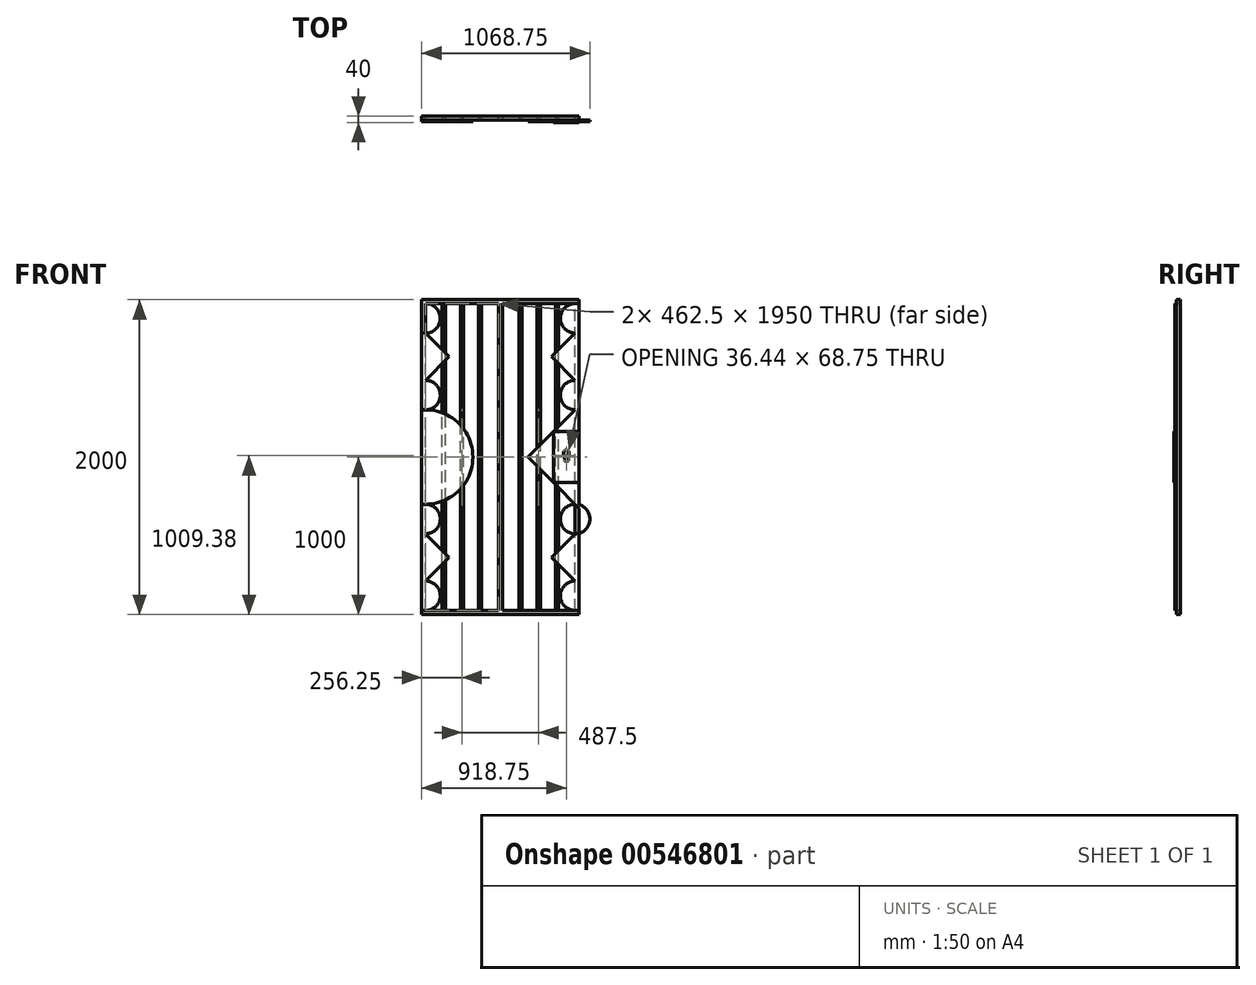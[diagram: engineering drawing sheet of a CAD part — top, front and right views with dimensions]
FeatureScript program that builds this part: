
annotation { "Feature Type Name" : "Feature", "Feature Type Description" : "" }
export const myFeature = defineFeature(function(context is Context, id is Id, definition is map)
    precondition{}
    {
        {
            var Q0;
            Q0=qCreatedBy(makeId("Front.planeOp"),FACE);
            var sketch = newSketch(context, id + "F0", { "sketchPlane" : qUnion([Q0])});
            skLineSegment(sketch, "E0.bottom", {"start": v(500, 12.5) * mm, "end": v(-500, 12.5) * mm});
            skLineSegment(sketch, "E0.top", {"start": v(500, -12.5) * mm, "end": v(-500, -12.5) * mm});
            skLineSegment(sketch, "E0.left", {"start": v(500, 12.5) * mm, "end": v(500, -12.5) * mm});
            skLineSegment(sketch, "E0.right", {"start": v(-500, 12.5) * mm, "end": v(-500, -12.5) * mm});
            skPoint(sketch, "E0.middle", {"position": v(0, 0) * mm});
            skLineSegment(sketch, "E1.bottom", {"start": v(-500, -12.5) * mm, "end": v(-475, -12.5) * mm});
            skLineSegment(sketch, "E1.top", {"start": v(-500, 1987.5) * mm, "end": v(-475, 1987.5) * mm});
            skLineSegment(sketch, "E1.left", {"start": v(-500, -12.5) * mm, "end": v(-500, 1987.5) * mm});
            skLineSegment(sketch, "E1.right", {"start": v(-475, -12.5) * mm, "end": v(-475, 1987.5) * mm});
            skLineSegment(sketch, "E2.bottom", {"start": v(500, -12.5) * mm, "end": v(475, -12.5) * mm});
            skLineSegment(sketch, "E2.top", {"start": v(500, 1987.5) * mm, "end": v(475, 1987.5) * mm});
            skLineSegment(sketch, "E2.left", {"start": v(500, -12.5) * mm, "end": v(500, 1987.5) * mm});
            skLineSegment(sketch, "E2.right", {"start": v(475, -12.5) * mm, "end": v(475, 1987.5) * mm});
            skLineSegment(sketch, "E3.bottom", {"start": v(500, 1987.5) * mm, "end": v(-500, 1987.5) * mm});
            skLineSegment(sketch, "E3.top", {"start": v(500, 1962.5) * mm, "end": v(-500, 1962.5) * mm});
            skLineSegment(sketch, "E3.left", {"start": v(500, 1987.5) * mm, "end": v(500, 1962.5) * mm});
            skLineSegment(sketch, "E3.right", {"start": v(-500, 1987.5) * mm, "end": v(-500, 1962.5) * mm});
            skSolve(sketch);
        }
        {
            var Q0;
            Q0 = qSketchRegion(id + "F0", true);
            extrude(context, id + "F1", {"entities" : qUnion([Q0]), "depth" : 25 * mm, "offsetDistance" : 25 * mm});
        }
        {
            var Q0;
            Q0=qCreatedBy(makeId("Top.planeOp"),FACE);
            var sketch = newSketch(context, id + "F2", { "sketchPlane" : qUnion([Q0])});
            skLineSegment(sketch, "E4.bottom", {"start": v(0, 0) * mm, "end": v(12.5, 0) * mm});
            skLineSegment(sketch, "E4.top", {"start": v(0, -25) * mm, "end": v(12.5, -25) * mm});
            skLineSegment(sketch, "E4.right", {"start": v(12.5, 0) * mm, "end": v(12.5, -25) * mm});
            skLineSegment(sketch, "E5.bottom", {"start": v(12.5, -25) * mm, "end": v(-12.5, -25) * mm});
            skLineSegment(sketch, "E5.top", {"start": v(12.5, 0) * mm, "end": v(-12.5, 0) * mm});
            skLineSegment(sketch, "E5.left", {"start": v(12.5, -25) * mm, "end": v(12.5, 0) * mm});
            skLineSegment(sketch, "E5.right", {"start": v(-12.5, -25) * mm, "end": v(-12.5, 0) * mm});
            skSolve(sketch);
        }
        {
            var Q0;
            Q0 = qSketchRegion(id + "F2", true);
            extrude(context, id + "F3", {"entities" : qUnion([Q0]), "operationType" : NewBodyOperationType.ADD, "depth" : 1975 * mm, "offsetDistance" : 25 * mm});
        }
        {
            var Q0;
            Q0=makeQuery(id+"F3.boolean.opBoolean","MERGE",FACE,{"derivedFrom":[makeQuery(id+"F1.opExtrude","CAP_FACE",FACE,{"disambiguationData":[OSD([sQuery(id+"F0.wireOp",EDGE,"E0.bottom"),sQuery(id+"F0.wireOp",EDGE,"E0.top"),sQuery(id+"F0.wireOp",EDGE,"E1.bottom"),sQuery(id+"F0.wireOp",EDGE,"E1.left"),sQuery(id+"F0.wireOp",EDGE,"E1.right"),sQuery(id+"F0.wireOp",EDGE,"E2.bottom"),sQuery(id+"F0.wireOp",EDGE,"E2.left"),sQuery(id+"F0.wireOp",EDGE,"E2.right"),sQuery(id+"F0.wireOp",EDGE,"E3.bottom"),sQuery(id+"F0.wireOp",EDGE,"E3.top"),sQuery(id+"F0.wireOp",EDGE,"E3.left"),sQuery(id+"F0.wireOp",EDGE,"E3.right")])],"isStart":false}),makeQuery(id+"F3.opExtrude","SWEPT_FACE",FACE,{"disambiguationData":[OSD([sQuery(id+"F2.wireOp",EDGE,"E5.bottom")])]})]});
            var sketch = newSketch(context, id + "F4", { "sketchPlane" : qUnion([Q0])});
            skLineSegment(sketch, "E6", {"start": v(475, 987.5) * mm, "end": v(475, 1187.5) * mm, "construction": true});
            skLineSegment(sketch, "E7", {"start": v(475, 987.5) * mm, "end": v(475, 787.5) * mm, "construction": true});
            skLineSegment(sketch, "E8", {"start": v(475, 987.5) * mm, "end": v(275, 987.5) * mm, "construction": true});
            skLineSegment(sketch, "E9", {"start": v(275, 987.5) * mm, "end": v(175, 987.5) * mm, "construction": true});
            skLineSegment(sketch, "E10", {"start": v(475, 1187.5) * mm, "end": v(475, 1287.5) * mm, "construction": true});
            skLineSegment(sketch, "E11", {"start": v(475, 787.5) * mm, "end": v(475, 687.5) * mm, "construction": true});
            skLineSegment(sketch, "E12", {"start": v(475, 687.5) * mm, "end": v(175, 987.5) * mm});
            skLineSegment(sketch, "E13", {"start": v(475, 1287.5) * mm, "end": v(175, 987.5) * mm});
            skCircle(sketch, "E14", {"center": v(-475, 987.5) * mm, "radius": 300 * mm});
            skLineSegment(sketch, "E15", {"start": v(475, 1287.5) * mm, "end": v(500, 1312.5) * mm});
            skLineSegment(sketch, "E16", {"start": v(175, 987.5) * mm, "end": v(505.2, 657.3) * mm});
            skLineSegment(sketch, "E17", {"start": v(475, 12.5) * mm, "end": v(500, 12.5) * mm, "construction": true});
            skLineSegment(sketch, "E18", {"start": v(-475, 12.5) * mm, "end": v(-500, 12.5) * mm, "construction": true});
            skLineSegment(sketch, "E19", {"start": v(475, 1962.5) * mm, "end": v(500, 1962.5) * mm, "construction": true});
            skLineSegment(sketch, "E20", {"start": v(-475, 1962.5) * mm, "end": v(-500, 1962.5) * mm, "construction": true});
            skLineSegment(sketch, "E21", {"start": v(-475, 12.5) * mm, "end": v(-475, 687.5) * mm, "construction": true});
            skLineSegment(sketch, "E22", {"start": v(475, 12.5) * mm, "end": v(475, 687.5) * mm, "construction": true});
            skLineSegment(sketch, "E23", {"start": v(475, 1287.5) * mm, "end": v(475, 1962.5) * mm, "construction": true});
            skLineSegment(sketch, "E24", {"start": v(-475, 1962.5) * mm, "end": v(-475, 1287.5) * mm, "construction": true});
            skLineSegment(sketch, "E25", {"start": v(-475, 350) * mm, "end": v(-500, 350) * mm, "construction": true});
            skLineSegment(sketch, "E26", {"start": v(-475, 350) * mm, "end": v(-475, 500) * mm});
            skLineSegment(sketch, "E27", {"start": v(-475, 350) * mm, "end": v(-325, 350) * mm});
            skLineSegment(sketch, "E28", {"start": v(-475, 350) * mm, "end": v(-475, 200) * mm});
            skLineSegment(sketch, "E29", {"start": v(-475, 200) * mm, "end": v(-325, 350) * mm});
            skLineSegment(sketch, "E30", {"start": v(-325, 350) * mm, "end": v(-475, 500) * mm});
            skLineSegment(sketch, "E31", {"start": v(-325, 350) * mm, "end": v(-500, 525) * mm});
            skLineSegment(sketch, "E32", {"start": v(-325, 350) * mm, "end": v(-500, 175) * mm});
            skLineSegment(sketch, "E33", {"start": v(475, 350) * mm, "end": v(475, 500) * mm});
            skLineSegment(sketch, "E34", {"start": v(475, 350) * mm, "end": v(325, 350) * mm});
            skLineSegment(sketch, "E35", {"start": v(475, 350) * mm, "end": v(475, 200) * mm});
            skLineSegment(sketch, "E36", {"start": v(475, 200) * mm, "end": v(325, 350) * mm});
            skLineSegment(sketch, "E37", {"start": v(475, 500) * mm, "end": v(325, 350) * mm});
            skLineSegment(sketch, "E38", {"start": v(325, 350) * mm, "end": v(500, 175) * mm});
            skLineSegment(sketch, "E39", {"start": v(325, 350) * mm, "end": v(500, 525) * mm});
            skLineSegment(sketch, "E40", {"start": v(475, 1625) * mm, "end": v(325, 1625) * mm});
            skPoint(sketch, "E40.endSnap0", {"position": v(475, 1625) * mm});
            skLineSegment(sketch, "E41", {"start": v(475, 1625) * mm, "end": v(475, 1775) * mm});
            skLineSegment(sketch, "E42", {"start": v(475, 1775) * mm, "end": v(475, 1475) * mm});
            skLineSegment(sketch, "E43", {"start": v(475, 1475) * mm, "end": v(325, 1625) * mm});
            skLineSegment(sketch, "E44", {"start": v(475, 1775) * mm, "end": v(325, 1625) * mm});
            skLineSegment(sketch, "E45", {"start": v(325, 1625) * mm, "end": v(500, 1450) * mm});
            skLineSegment(sketch, "E46", {"start": v(325, 1625) * mm, "end": v(500, 1800) * mm});
            skLineSegment(sketch, "E47", {"start": v(-475, 1625) * mm, "end": v(-325, 1625) * mm});
            skLineSegment(sketch, "E48", {"start": v(-475, 1625) * mm, "end": v(-475, 1475) * mm});
            skLineSegment(sketch, "E49", {"start": v(-475, 1475) * mm, "end": v(-475, 1775) * mm});
            skLineSegment(sketch, "E50", {"start": v(-475, 1775) * mm, "end": v(-325, 1625) * mm});
            skLineSegment(sketch, "E51", {"start": v(-325, 1625) * mm, "end": v(-500, 1800) * mm});
            skLineSegment(sketch, "E52", {"start": v(-500, 1800) * mm, "end": v(-325, 1625) * mm});
            skLineSegment(sketch, "E53", {"start": v(-325, 1625) * mm, "end": v(-500, 1450) * mm});
            skLineSegment(sketch, "E54", {"start": v(500, 662.5) * mm, "end": v(500, 525) * mm});
            skLineSegment(sketch, "E55", {"start": v(475, 687.5) * mm, "end": v(475, 500) * mm, "construction": true});
            skCircle(sketch, "E56", {"center": v(475, 593.75) * mm, "radius": 93.75 * mm});
            skLineSegment(sketch, "E57", {"start": v(475, 200) * mm, "end": v(475, 12.5) * mm, "construction": true});
            skCircle(sketch, "E58", {"center": v(475, 106.25) * mm, "radius": 93.75 * mm});
            skLineSegment(sketch, "E59", {"start": v(475, 1475) * mm, "end": v(475, 1287.5) * mm, "construction": true});
            skLineSegment(sketch, "E60", {"start": v(475, 1775) * mm, "end": v(475, 1962.5) * mm, "construction": true});
            skLineSegment(sketch, "E61", {"start": v(-475, 1962.5) * mm, "end": v(-475, 1775) * mm, "construction": true});
            skLineSegment(sketch, "E62", {"start": v(-475, 1475) * mm, "end": v(-475, 1287.5) * mm, "construction": true});
            skLineSegment(sketch, "E63", {"start": v(-475, 687.5) * mm, "end": v(-475, 500) * mm, "construction": true});
            skLineSegment(sketch, "E64", {"start": v(-475, 200) * mm, "end": v(-475, 12.5) * mm, "construction": true});
            skCircle(sketch, "E65", {"center": v(-475, 106.25) * mm, "radius": 93.75 * mm});
            skCircle(sketch, "E66", {"center": v(-475, 593.75) * mm, "radius": 93.75 * mm});
            skCircle(sketch, "E67", {"center": v(-475, 1381.25) * mm, "radius": 93.75 * mm});
            skCircle(sketch, "E68", {"center": v(-475, 1868.75) * mm, "radius": 93.75 * mm});
            skCircle(sketch, "E69", {"center": v(475, 1868.75) * mm, "radius": 93.75 * mm});
            skCircle(sketch, "E70", {"center": v(475, 1381.25) * mm, "radius": 93.75 * mm});
            skSolve(sketch);
        }
        {
            var Q0;
            {var subQ0=sQuery(id+"F4.wireOp",EDGE,"E14");var subQ1=makeQuery(id+"F1.opExtrude","CAP_EDGE",EDGE,{"disambiguationData":[OSD([sQuery(id+"F0.wireOp",EDGE,"E1.left"),sQuery(id+"F0.wireOp",EDGE,"E3.right")])],"isStart":false});var subQ2=makeQuery(id+"F4.imprint","INTERSECT",VERTEX,{"disambiguationData":[OD(0.0)],"derivedFrom":[subQ1,subQ0]});Q0=makeQuery(id+"F4.imprint","IMPRINT",FACE,{"disambiguationData":[TD([[makeQuery(id+"F4.imprint","IMPRINT",EDGE,{"disambiguationData":[TD([[subQ2,1.0]])],"derivedFrom":subQ0}),1.0]])]});}
            var Q1;
            {var subQ0=sQuery(id+"F4.wireOp",EDGE,"E14");var subQ1=makeQuery(id+"F1.opExtrude","CAP_EDGE",EDGE,{"disambiguationData":[OSD([sQuery(id+"F0.wireOp",EDGE,"E1.right")])],"isStart":false});var subQ2=makeQuery(id+"F4.imprint","INTERSECT",VERTEX,{"derivedFrom":[subQ1,subQ0,sQuery(id+"F4.wireOp",EDGE,"E67")]});Q1=makeQuery(id+"F4.imprint","IMPRINT",FACE,{"disambiguationData":[TD([[makeQuery(id+"F4.imprint","IMPRINT",EDGE,{"disambiguationData":[TD([[subQ2,1.0]])],"derivedFrom":subQ0}),1.0]])]});}
            var Q2;
            {var subQ1=sQuery(id+"F4.wireOp",EDGE,"E26");Q2=makeQuery(id+"F4.imprint","IMPRINT",FACE,{"disambiguationData":[TD([[makeQuery(id+"F4.imprint","IMPRINT",EDGE,{"derivedFrom":subQ1}),1.0]])]});}
            var Q3;
            {var subQ0=sQuery(id+"F4.wireOp",EDGE,"E26");Q3=makeQuery(id+"F4.imprint","IMPRINT",FACE,{"disambiguationData":[TD([[makeQuery(id+"F4.imprint","IMPRINT",EDGE,{"derivedFrom":subQ0}),-1.0]])]});}
            var Q4;
            {var subQ0=sQuery(id+"F4.wireOp",EDGE,"E27");Q4=makeQuery(id+"F4.imprint","IMPRINT",FACE,{"disambiguationData":[TD([[makeQuery(id+"F4.imprint","IMPRINT",EDGE,{"derivedFrom":subQ0}),-1.0]])]});}
            var Q5;
            {var subQ0=sQuery(id+"F4.wireOp",EDGE,"E13");Q5=makeQuery(id+"F4.imprint","IMPRINT",FACE,{"disambiguationData":[TD([[makeQuery(id+"F4.imprint","IMPRINT",EDGE,{"derivedFrom":subQ0}),1.0]])]});}
            var Q6;
            {var subQ0=sQuery(id+"F4.wireOp",EDGE,"E15");Q6=makeQuery(id+"F4.imprint","IMPRINT",FACE,{"disambiguationData":[TD([[makeQuery(id+"F4.imprint","IMPRINT",EDGE,{"derivedFrom":subQ0}),-1.0]])]});}
            var Q7;
            {var subQ6=sQuery(id+"F4.wireOp",EDGE,"E33");Q7=makeQuery(id+"F4.imprint","IMPRINT",FACE,{"disambiguationData":[TD([[makeQuery(id+"F4.imprint","IMPRINT",EDGE,{"derivedFrom":subQ6}),-1.0]])]});}
            var Q8;
            {var subQ0=sQuery(id+"F4.wireOp",EDGE,"E33");Q8=makeQuery(id+"F4.imprint","IMPRINT",FACE,{"disambiguationData":[TD([[makeQuery(id+"F4.imprint","IMPRINT",EDGE,{"derivedFrom":subQ0}),1.0]])]});}
            var Q9;
            {var subQ0=sQuery(id+"F4.wireOp",EDGE,"E34");Q9=makeQuery(id+"F4.imprint","IMPRINT",FACE,{"disambiguationData":[TD([[makeQuery(id+"F4.imprint","IMPRINT",EDGE,{"derivedFrom":subQ0}),1.0]])]});}
            var Q10;
            {var subQ1=sQuery(id+"F4.wireOp",EDGE,"E42");var subQ6=makeQuery(id+"F4.imprint","INTERSECT",VERTEX,{"derivedFrom":[sQuery(id+"F4.wireOp",EDGE,"E40"),subQ1]});Q10=makeQuery(id+"F4.imprint","IMPRINT",FACE,{"disambiguationData":[TD([[makeQuery(id+"F4.imprint","IMPRINT",EDGE,{"disambiguationData":[TD([[subQ6,1.0]])],"derivedFrom":subQ1}),-1.0]])]});}
            var Q11;
            {var subQ0=sQuery(id+"F4.wireOp",EDGE,"E40");Q11=makeQuery(id+"F4.imprint","IMPRINT",FACE,{"disambiguationData":[TD([[makeQuery(id+"F4.imprint","IMPRINT",EDGE,{"derivedFrom":subQ0}),-1.0]])]});}
            var Q12;
            {var subQ0=sQuery(id+"F4.wireOp",EDGE,"E40");Q12=makeQuery(id+"F4.imprint","IMPRINT",FACE,{"disambiguationData":[TD([[makeQuery(id+"F4.imprint","IMPRINT",EDGE,{"derivedFrom":subQ0}),1.0]])]});}
            var Q13;
            {var subQ1=sQuery(id+"F4.wireOp",EDGE,"E49");var subQ9=makeQuery(id+"F4.imprint","INTERSECT",VERTEX,{"derivedFrom":[sQuery(id+"F4.wireOp",EDGE,"E47"),subQ1]});Q13=makeQuery(id+"F4.imprint","IMPRINT",FACE,{"disambiguationData":[TD([[makeQuery(id+"F4.imprint","IMPRINT",EDGE,{"disambiguationData":[TD([[subQ9,1.0]])],"derivedFrom":subQ1}),1.0]])]});}
            var Q14;
            {var subQ0=sQuery(id+"F4.wireOp",EDGE,"E47");Q14=makeQuery(id+"F4.imprint","IMPRINT",FACE,{"disambiguationData":[TD([[makeQuery(id+"F4.imprint","IMPRINT",EDGE,{"derivedFrom":subQ0}),-1.0]])]});}
            var Q15;
            {var subQ0=sQuery(id+"F4.wireOp",EDGE,"E47");Q15=makeQuery(id+"F4.imprint","IMPRINT",FACE,{"disambiguationData":[TD([[makeQuery(id+"F4.imprint","IMPRINT",EDGE,{"derivedFrom":subQ0}),1.0]])]});}
            var Q16;
            {var subQ0=sQuery(id+"F4.wireOp",EDGE,"E54");Q16=makeQuery(id+"F4.imprint","IMPRINT",FACE,{"disambiguationData":[TD([[makeQuery(id+"F4.imprint","IMPRINT",EDGE,{"derivedFrom":subQ0}),1.0]])]});}
            var Q17;
            {var subQ0=sQuery(id+"F4.wireOp",EDGE,"E56");var subQ1=makeQuery(id+"F1.opExtrude","CAP_EDGE",EDGE,{"disambiguationData":[OSD([sQuery(id+"F0.wireOp",EDGE,"E2.right")])],"isStart":false});var subQ3=makeQuery(id+"F4.imprint","INTERSECT",VERTEX,{"derivedFrom":[subQ1,sQuery(id+"F4.wireOp",EDGE,"E16"),subQ0]});Q17=makeQuery(id+"F4.imprint","IMPRINT",FACE,{"disambiguationData":[TD([[makeQuery(id+"F4.imprint","IMPRINT",EDGE,{"disambiguationData":[TD([[subQ3,-1.0]])],"derivedFrom":subQ0}),1.0]])]});}
            var Q18;
            {var subQ1=sQuery(id+"F4.wireOp",EDGE,"E38");var subQ5=sQuery(id+"F0.wireOp",EDGE,"E3.left");var subQ6=sQuery(id+"F0.wireOp",EDGE,"E2.left");var subQ7=makeQuery(id+"F1.opExtrude","CAP_EDGE",EDGE,{"disambiguationData":[OSD([subQ6,subQ5])],"isStart":false});var subQ8=makeQuery(id+"F4.imprint","INTERSECT",VERTEX,{"derivedFrom":[subQ7,subQ1]});Q18=makeQuery(id+"F4.imprint","IMPRINT",FACE,{"disambiguationData":[TD([[makeQuery(id+"F4.imprint","IMPRINT",EDGE,{"disambiguationData":[TD([[subQ8,1.0]])],"derivedFrom":subQ1}),-1.0]])]});}
            var Q19;
            {var subQ0=sQuery(id+"F4.wireOp",EDGE,"E58");var subQ1=sQuery(id+"F0.wireOp",EDGE,"E2.right");var subQ3=makeQuery(id+"F1.opExtrude","CAP_EDGE",EDGE,{"disambiguationData":[OSD([subQ1])],"isStart":false});var subQ5=makeQuery(id+"F4.imprint","INTERSECT",VERTEX,{"derivedFrom":[subQ3,sQuery(id+"F4.wireOp",EDGE,"E35"),sQuery(id+"F4.wireOp",EDGE,"E38"),subQ0]});Q19=makeQuery(id+"F4.imprint","IMPRINT",FACE,{"disambiguationData":[TD([[makeQuery(id+"F4.imprint","IMPRINT",EDGE,{"disambiguationData":[TD([[subQ5,-1.0]])],"derivedFrom":subQ0}),1.0]])]});}
            var Q20;
            {var subQ1=sQuery(id+"F4.wireOp",EDGE,"E32");var subQ5=sQuery(id+"F0.wireOp",EDGE,"E3.right");var subQ6=sQuery(id+"F0.wireOp",EDGE,"E1.left");var subQ7=makeQuery(id+"F1.opExtrude","CAP_EDGE",EDGE,{"disambiguationData":[OSD([subQ6,subQ5])],"isStart":false});var subQ8=makeQuery(id+"F4.imprint","INTERSECT",VERTEX,{"derivedFrom":[subQ7,subQ1]});Q20=makeQuery(id+"F4.imprint","IMPRINT",FACE,{"disambiguationData":[TD([[makeQuery(id+"F4.imprint","IMPRINT",EDGE,{"disambiguationData":[TD([[subQ8,1.0]])],"derivedFrom":subQ1}),1.0]])]});}
            var Q21;
            {var subQ0=sQuery(id+"F4.wireOp",EDGE,"E65");var subQ1=sQuery(id+"F0.wireOp",EDGE,"E1.right");var subQ3=makeQuery(id+"F1.opExtrude","CAP_EDGE",EDGE,{"disambiguationData":[OSD([subQ1])],"isStart":false});var subQ5=makeQuery(id+"F4.imprint","INTERSECT",VERTEX,{"derivedFrom":[subQ3,sQuery(id+"F4.wireOp",EDGE,"E28"),sQuery(id+"F4.wireOp",EDGE,"E32"),subQ0]});Q21=makeQuery(id+"F4.imprint","IMPRINT",FACE,{"disambiguationData":[TD([[makeQuery(id+"F4.imprint","IMPRINT",EDGE,{"disambiguationData":[TD([[subQ5,1.0]])],"derivedFrom":subQ0}),1.0]])]});}
            var Q22;
            {var subQ0=sQuery(id+"F4.wireOp",EDGE,"E66");var subQ1=makeQuery(id+"F1.opExtrude","CAP_EDGE",EDGE,{"disambiguationData":[OSD([sQuery(id+"F0.wireOp",EDGE,"E1.right")])],"isStart":false});var subQ3=makeQuery(id+"F4.imprint","INTERSECT",VERTEX,{"derivedFrom":[subQ1,sQuery(id+"F4.wireOp",EDGE,"E14"),subQ0]});Q22=makeQuery(id+"F4.imprint","IMPRINT",FACE,{"disambiguationData":[TD([[makeQuery(id+"F4.imprint","IMPRINT",EDGE,{"disambiguationData":[TD([[subQ3,1.0]])],"derivedFrom":subQ0}),1.0]])]});}
            var Q23;
            {var subQ0=sQuery(id+"F4.wireOp",EDGE,"E66");var subQ4=makeQuery(id+"F1.opExtrude","CAP_EDGE",EDGE,{"disambiguationData":[OSD([sQuery(id+"F0.wireOp",EDGE,"E1.left"),sQuery(id+"F0.wireOp",EDGE,"E3.right")])],"isStart":false});var subQ7=makeQuery(id+"F4.imprint","INTERSECT",VERTEX,{"disambiguationData":[OD(0.0)],"derivedFrom":[subQ4,subQ0]});Q23=makeQuery(id+"F4.imprint","IMPRINT",FACE,{"disambiguationData":[TD([[makeQuery(id+"F4.imprint","IMPRINT",EDGE,{"disambiguationData":[TD([[subQ7,1.0]])],"derivedFrom":subQ0}),1.0]])]});}
            var Q24;
            {var subQ0=sQuery(id+"F4.wireOp",EDGE,"E67");var subQ4=makeQuery(id+"F1.opExtrude","CAP_EDGE",EDGE,{"disambiguationData":[OSD([sQuery(id+"F0.wireOp",EDGE,"E1.left"),sQuery(id+"F0.wireOp",EDGE,"E3.right")])],"isStart":false});var subQ6=makeQuery(id+"F4.imprint","INTERSECT",VERTEX,{"disambiguationData":[OD(1.0)],"derivedFrom":[subQ4,subQ0]});Q24=makeQuery(id+"F4.imprint","IMPRINT",FACE,{"disambiguationData":[TD([[makeQuery(id+"F4.imprint","IMPRINT",EDGE,{"disambiguationData":[TD([[subQ6,-1.0]])],"derivedFrom":subQ0}),1.0]])]});}
            var Q25;
            {var subQ0=sQuery(id+"F4.wireOp",EDGE,"E67");var subQ1=makeQuery(id+"F1.opExtrude","CAP_EDGE",EDGE,{"disambiguationData":[OSD([sQuery(id+"F0.wireOp",EDGE,"E1.right")])],"isStart":false});var subQ3=makeQuery(id+"F4.imprint","INTERSECT",VERTEX,{"derivedFrom":[subQ1,sQuery(id+"F4.wireOp",EDGE,"E14"),subQ0]});Q25=makeQuery(id+"F4.imprint","IMPRINT",FACE,{"disambiguationData":[TD([[makeQuery(id+"F4.imprint","IMPRINT",EDGE,{"disambiguationData":[TD([[subQ3,-1.0]])],"derivedFrom":subQ0}),1.0]])]});}
            var Q26;
            {var subQ0=sQuery(id+"F4.wireOp",EDGE,"E70");var subQ1=makeQuery(id+"F1.opExtrude","CAP_EDGE",EDGE,{"disambiguationData":[OSD([sQuery(id+"F0.wireOp",EDGE,"E2.right")])],"isStart":false});var subQ2=makeQuery(id+"F4.imprint","INTERSECT",VERTEX,{"derivedFrom":[subQ1,sQuery(id+"F4.wireOp",EDGE,"E13"),sQuery(id+"F4.wireOp",EDGE,"E15"),subQ0]});Q26=makeQuery(id+"F4.imprint","IMPRINT",FACE,{"disambiguationData":[TD([[makeQuery(id+"F4.imprint","IMPRINT",EDGE,{"disambiguationData":[TD([[subQ2,1.0]])],"derivedFrom":subQ0}),1.0]])]});}
            var Q27;
            {var subQ0=sQuery(id+"F4.wireOp",EDGE,"E15");Q27=makeQuery(id+"F4.imprint","IMPRINT",FACE,{"disambiguationData":[TD([[makeQuery(id+"F4.imprint","IMPRINT",EDGE,{"derivedFrom":subQ0}),1.0]])]});}
            var Q28;
            {var subQ0=sQuery(id+"F4.wireOp",EDGE,"E69");var subQ2=sQuery(id+"F0.wireOp",EDGE,"E2.right");var subQ3=makeQuery(id+"F1.opExtrude","CAP_EDGE",EDGE,{"disambiguationData":[OSD([subQ2])],"isStart":false});var subQ5=makeQuery(id+"F4.imprint","INTERSECT",VERTEX,{"derivedFrom":[subQ3,sQuery(id+"F4.wireOp",EDGE,"E42"),sQuery(id+"F4.wireOp",EDGE,"E46"),subQ0]});Q28=makeQuery(id+"F4.imprint","IMPRINT",FACE,{"disambiguationData":[TD([[makeQuery(id+"F4.imprint","IMPRINT",EDGE,{"disambiguationData":[TD([[subQ5,1.0]])],"derivedFrom":subQ0}),1.0]])]});}
            var Q29;
            {var subQ1=sQuery(id+"F4.wireOp",EDGE,"E46");var subQ5=sQuery(id+"F0.wireOp",EDGE,"E3.left");var subQ6=sQuery(id+"F0.wireOp",EDGE,"E2.left");var subQ7=makeQuery(id+"F1.opExtrude","CAP_EDGE",EDGE,{"disambiguationData":[OSD([subQ6,subQ5])],"isStart":false});var subQ8=makeQuery(id+"F4.imprint","INTERSECT",VERTEX,{"derivedFrom":[subQ7,subQ1]});Q29=makeQuery(id+"F4.imprint","IMPRINT",FACE,{"disambiguationData":[TD([[makeQuery(id+"F4.imprint","IMPRINT",EDGE,{"disambiguationData":[TD([[subQ8,1.0]])],"derivedFrom":subQ1}),1.0]])]});}
            var Q30;
            {var subQ0=sQuery(id+"F4.wireOp",EDGE,"E68");var subQ2=sQuery(id+"F0.wireOp",EDGE,"E1.right");var subQ3=makeQuery(id+"F1.opExtrude","CAP_EDGE",EDGE,{"disambiguationData":[OSD([subQ2])],"isStart":false});var subQ5=makeQuery(id+"F4.imprint","INTERSECT",VERTEX,{"derivedFrom":[subQ3,sQuery(id+"F4.wireOp",EDGE,"E49"),sQuery(id+"F4.wireOp",EDGE,"E52"),subQ0]});Q30=makeQuery(id+"F4.imprint","IMPRINT",FACE,{"disambiguationData":[TD([[makeQuery(id+"F4.imprint","IMPRINT",EDGE,{"disambiguationData":[TD([[subQ5,-1.0]])],"derivedFrom":subQ0}),1.0]])]});}
            var Q31;
            {var subQ1=sQuery(id+"F4.wireOp",EDGE,"E52");var subQ5=sQuery(id+"F0.wireOp",EDGE,"E3.right");var subQ6=sQuery(id+"F0.wireOp",EDGE,"E1.left");var subQ7=makeQuery(id+"F1.opExtrude","CAP_EDGE",EDGE,{"disambiguationData":[OSD([subQ6,subQ5])],"isStart":false});var subQ8=makeQuery(id+"F4.imprint","INTERSECT",VERTEX,{"derivedFrom":[subQ7,subQ1]});Q31=makeQuery(id+"F4.imprint","IMPRINT",FACE,{"disambiguationData":[TD([[makeQuery(id+"F4.imprint","IMPRINT",EDGE,{"disambiguationData":[TD([[subQ8,-1.0]])],"derivedFrom":subQ1}),1.0]])]});}
            var Q32;
            {var subQ1=sQuery(id+"F4.wireOp",EDGE,"E53");var subQ3=makeQuery(id+"F1.opExtrude","CAP_EDGE",EDGE,{"disambiguationData":[OSD([sQuery(id+"F0.wireOp",EDGE,"E1.left"),sQuery(id+"F0.wireOp",EDGE,"E3.right")])],"isStart":false});var subQ4=makeQuery(id+"F4.imprint","INTERSECT",VERTEX,{"derivedFrom":[subQ3,subQ1]});Q32=makeQuery(id+"F4.imprint","IMPRINT",FACE,{"disambiguationData":[TD([[makeQuery(id+"F4.imprint","IMPRINT",EDGE,{"disambiguationData":[TD([[subQ4,1.0]])],"derivedFrom":subQ1}),-1.0]])]});}
            var Q33;
            {var subQ1=sQuery(id+"F4.wireOp",EDGE,"E52");var subQ3=makeQuery(id+"F1.opExtrude","CAP_EDGE",EDGE,{"disambiguationData":[OSD([sQuery(id+"F0.wireOp",EDGE,"E1.left"),sQuery(id+"F0.wireOp",EDGE,"E3.right")])],"isStart":false});var subQ4=makeQuery(id+"F4.imprint","INTERSECT",VERTEX,{"derivedFrom":[subQ3,subQ1]});Q33=makeQuery(id+"F4.imprint","IMPRINT",FACE,{"disambiguationData":[TD([[makeQuery(id+"F4.imprint","IMPRINT",EDGE,{"disambiguationData":[TD([[subQ4,-1.0]])],"derivedFrom":subQ1}),-1.0]])]});}
            var Q34;
            {var subQ1=sQuery(id+"F4.wireOp",EDGE,"E46");var subQ3=makeQuery(id+"F1.opExtrude","CAP_EDGE",EDGE,{"disambiguationData":[OSD([sQuery(id+"F0.wireOp",EDGE,"E2.left"),sQuery(id+"F0.wireOp",EDGE,"E3.left")])],"isStart":false});var subQ4=makeQuery(id+"F4.imprint","INTERSECT",VERTEX,{"derivedFrom":[subQ3,subQ1]});Q34=makeQuery(id+"F4.imprint","IMPRINT",FACE,{"disambiguationData":[TD([[makeQuery(id+"F4.imprint","IMPRINT",EDGE,{"disambiguationData":[TD([[subQ4,1.0]])],"derivedFrom":subQ1}),-1.0]])]});}
            var Q35;
            {var subQ1=sQuery(id+"F4.wireOp",EDGE,"E45");var subQ3=makeQuery(id+"F1.opExtrude","CAP_EDGE",EDGE,{"disambiguationData":[OSD([sQuery(id+"F0.wireOp",EDGE,"E2.left"),sQuery(id+"F0.wireOp",EDGE,"E3.left")])],"isStart":false});var subQ4=makeQuery(id+"F4.imprint","INTERSECT",VERTEX,{"derivedFrom":[subQ3,subQ1]});Q35=makeQuery(id+"F4.imprint","IMPRINT",FACE,{"disambiguationData":[TD([[makeQuery(id+"F4.imprint","IMPRINT",EDGE,{"disambiguationData":[TD([[subQ4,1.0]])],"derivedFrom":subQ1}),1.0]])]});}
            var Q36;
            {var subQ1=sQuery(id+"F4.wireOp",EDGE,"E31");var subQ3=makeQuery(id+"F1.opExtrude","CAP_EDGE",EDGE,{"disambiguationData":[OSD([sQuery(id+"F0.wireOp",EDGE,"E1.left"),sQuery(id+"F0.wireOp",EDGE,"E3.right")])],"isStart":false});var subQ4=makeQuery(id+"F4.imprint","INTERSECT",VERTEX,{"derivedFrom":[subQ3,subQ1]});Q36=makeQuery(id+"F4.imprint","IMPRINT",FACE,{"disambiguationData":[TD([[makeQuery(id+"F4.imprint","IMPRINT",EDGE,{"disambiguationData":[TD([[subQ4,1.0]])],"derivedFrom":subQ1}),1.0]])]});}
            var Q37;
            {var subQ1=sQuery(id+"F4.wireOp",EDGE,"E32");var subQ3=makeQuery(id+"F1.opExtrude","CAP_EDGE",EDGE,{"disambiguationData":[OSD([sQuery(id+"F0.wireOp",EDGE,"E1.left"),sQuery(id+"F0.wireOp",EDGE,"E3.right")])],"isStart":false});var subQ4=makeQuery(id+"F4.imprint","INTERSECT",VERTEX,{"derivedFrom":[subQ3,subQ1]});Q37=makeQuery(id+"F4.imprint","IMPRINT",FACE,{"disambiguationData":[TD([[makeQuery(id+"F4.imprint","IMPRINT",EDGE,{"disambiguationData":[TD([[subQ4,1.0]])],"derivedFrom":subQ1}),-1.0]])]});}
            var Q38;
            {var subQ0=sQuery(id+"F4.wireOp",EDGE,"E56");var subQ3=makeQuery(id+"F1.opExtrude","CAP_EDGE",EDGE,{"disambiguationData":[OSD([sQuery(id+"F0.wireOp",EDGE,"E2.left"),sQuery(id+"F0.wireOp",EDGE,"E3.left")])],"isStart":false});var subQ5=makeQuery(id+"F4.imprint","INTERSECT",VERTEX,{"disambiguationData":[OD(1.0)],"derivedFrom":[subQ3,subQ0]});Q38=makeQuery(id+"F4.imprint","IMPRINT",FACE,{"disambiguationData":[TD([[makeQuery(id+"F4.imprint","IMPRINT",EDGE,{"disambiguationData":[TD([[subQ5,1.0]])],"derivedFrom":subQ0}),1.0]])]});}
            var Q39;
            {var subQ1=sQuery(id+"F4.wireOp",EDGE,"E38");var subQ3=makeQuery(id+"F1.opExtrude","CAP_EDGE",EDGE,{"disambiguationData":[OSD([sQuery(id+"F0.wireOp",EDGE,"E2.left"),sQuery(id+"F0.wireOp",EDGE,"E3.left")])],"isStart":false});var subQ4=makeQuery(id+"F4.imprint","INTERSECT",VERTEX,{"derivedFrom":[subQ3,subQ1]});Q39=makeQuery(id+"F4.imprint","IMPRINT",FACE,{"disambiguationData":[TD([[makeQuery(id+"F4.imprint","IMPRINT",EDGE,{"disambiguationData":[TD([[subQ4,1.0]])],"derivedFrom":subQ1}),1.0]])]});}
            var Q40;
            {var subQ0=sQuery(id+"F4.wireOp",EDGE,"E56");var subQ1=makeQuery(id+"F1.opExtrude","CAP_EDGE",EDGE,{"disambiguationData":[OSD([sQuery(id+"F0.wireOp",EDGE,"E2.right")])],"isStart":false});var subQ2=makeQuery(id+"F4.imprint","INTERSECT",VERTEX,{"derivedFrom":[subQ1,sQuery(id+"F4.wireOp",EDGE,"E16"),subQ0]});Q40=makeQuery(id+"F4.imprint","IMPRINT",FACE,{"disambiguationData":[TD([[makeQuery(id+"F4.imprint","IMPRINT",EDGE,{"disambiguationData":[TD([[subQ2,1.0]])],"derivedFrom":subQ0}),-1.0]])]});}
            var Q41;
            {var subQ0=sQuery(id+"F4.wireOp",EDGE,"E16");var subQ3=sQuery(id+"F4.wireOp",EDGE,"E56");var subQ4=makeQuery(id+"F4.imprint","INTERSECT",VERTEX,{"derivedFrom":[makeQuery(id+"F1.opExtrude","CAP_EDGE",EDGE,{"disambiguationData":[OSD([sQuery(id+"F0.wireOp",EDGE,"E2.right")])],"isStart":false}),subQ0,subQ3]});Q41=makeQuery(id+"F4.imprint","IMPRINT",FACE,{"disambiguationData":[TD([[makeQuery(id+"F4.imprint","IMPRINT",EDGE,{"disambiguationData":[TD([[subQ4,1.0]])],"derivedFrom":subQ3}),1.0]])]});}
            extrude(context, id + "F5", {"entities" : qUnion([Q0, Q1, Q2, Q3, Q4, Q5, Q6, Q7, Q8, Q9, Q10, Q11, Q12, Q13, Q14, Q15, Q16, Q17, Q18, Q19, Q20, Q21, Q22, Q23, Q24, Q25, Q26, Q27, Q28, Q29, Q30, Q31, Q32, Q33, Q34, Q35, Q36, Q37, Q38, Q39, Q40, Q41]), "depth" : 10 * mm, "offsetDistance" : 25 * mm});
        }
        {
            var Q0;
            {var subQ2=sQuery(id+"F0.wireOp",EDGE,"E3.top");var subQ7=sQuery(id+"F0.wireOp",EDGE,"E1.right");Q0=makeQuery(id+"F3.boolean.opBoolean","SPLIT",FACE,{"disambiguationData":[TD([makeQuery(id+"F1.opExtrude","SWEPT_FACE",FACE,{"disambiguationData":[OSD([subQ7])]})])],"derivedFrom":makeQuery(id+"F1.opExtrude","SWEPT_FACE",FACE,{"disambiguationData":[OSD([subQ2])]})});}
            var sketch = newSketch(context, id + "F6", { "sketchPlane" : qUnion([Q0])});
            skLineSegment(sketch, "E71", {"start": v(-475, 25) * mm, "end": v(-12.5, 25) * mm});
            skLineSegment(sketch, "E72", {"start": v(-12.5, 25) * mm, "end": v(-243.75, 25) * mm});
            skLineSegment(sketch, "E73", {"start": v(-243.75, 25) * mm, "end": v(-243.75, 0) * mm});
            skLineSegment(sketch, "E74", {"start": v(-243.75, 0) * mm, "end": v(-475, 0) * mm});
            skLineSegment(sketch, "E75", {"start": v(-243.75, 0) * mm, "end": v(-12.5, 0) * mm});
            skCircle(sketch, "E76", {"center": v(-243.75, 12.5) * mm, "radius": 10 * mm});
            skLineSegment(sketch, "E77", {"start": v(-128.12, 25) * mm, "end": v(-128.12, 0) * mm});
            skLineSegment(sketch, "E78", {"start": v(-359.38, 0) * mm, "end": v(-359.38, 25) * mm});
            skCircle(sketch, "E79", {"center": v(-359.38, 12.5) * mm, "radius": 10 * mm});
            skCircle(sketch, "E80", {"center": v(-128.12, 12.5) * mm, "radius": 10 * mm});
            skSolve(sketch);
        }
        {
            var Q0;
            {var subQ0=sQuery(id+"F6.wireOp",EDGE,"E80");var subQ1=sQuery(id+"F6.wireOp",EDGE,"E77");var subQ2=makeQuery(id+"F6.imprint","INTERSECT",VERTEX,{"disambiguationData":[OD(0.0)],"derivedFrom":[subQ1,subQ0]});Q0=makeQuery(id+"F6.imprint","IMPRINT",FACE,{"disambiguationData":[TD([[makeQuery(id+"F6.imprint","IMPRINT",EDGE,{"disambiguationData":[TD([[subQ2,-1.0]])],"derivedFrom":subQ1}),-1.0]])]});}
            var Q1;
            {var subQ0=sQuery(id+"F6.wireOp",EDGE,"E80");var subQ1=sQuery(id+"F6.wireOp",EDGE,"E77");var subQ2=makeQuery(id+"F6.imprint","INTERSECT",VERTEX,{"disambiguationData":[OD(0.0)],"derivedFrom":[subQ1,subQ0]});Q1=makeQuery(id+"F6.imprint","IMPRINT",FACE,{"disambiguationData":[TD([[makeQuery(id+"F6.imprint","IMPRINT",EDGE,{"disambiguationData":[TD([[subQ2,-1.0]])],"derivedFrom":subQ1}),1.0]])]});}
            var Q2;
            {var subQ0=sQuery(id+"F6.wireOp",EDGE,"E79");var subQ1=sQuery(id+"F6.wireOp",EDGE,"E78");var subQ2=makeQuery(id+"F6.imprint","INTERSECT",VERTEX,{"disambiguationData":[OD(0.0)],"derivedFrom":[subQ1,subQ0]});Q2=makeQuery(id+"F6.imprint","IMPRINT",FACE,{"disambiguationData":[TD([[makeQuery(id+"F6.imprint","IMPRINT",EDGE,{"disambiguationData":[TD([[subQ2,-1.0]])],"derivedFrom":subQ1}),1.0]])]});}
            var Q3;
            {var subQ0=sQuery(id+"F6.wireOp",EDGE,"E79");var subQ1=sQuery(id+"F6.wireOp",EDGE,"E78");var subQ2=makeQuery(id+"F6.imprint","INTERSECT",VERTEX,{"disambiguationData":[OD(0.0)],"derivedFrom":[subQ1,subQ0]});Q3=makeQuery(id+"F6.imprint","IMPRINT",FACE,{"disambiguationData":[TD([[makeQuery(id+"F6.imprint","IMPRINT",EDGE,{"disambiguationData":[TD([[subQ2,-1.0]])],"derivedFrom":subQ1}),-1.0]])]});}
            var Q4;
            {var subQ0=sQuery(id+"F6.wireOp",EDGE,"E76");var subQ1=sQuery(id+"F6.wireOp",EDGE,"E73");var subQ2=makeQuery(id+"F6.imprint","INTERSECT",VERTEX,{"disambiguationData":[OD(0.0)],"derivedFrom":[subQ1,subQ0]});Q4=makeQuery(id+"F6.imprint","IMPRINT",FACE,{"disambiguationData":[TD([[makeQuery(id+"F6.imprint","IMPRINT",EDGE,{"disambiguationData":[TD([[subQ2,-1.0]])],"derivedFrom":subQ1}),1.0]])]});}
            var Q5;
            {var subQ0=sQuery(id+"F6.wireOp",EDGE,"E76");var subQ1=sQuery(id+"F6.wireOp",EDGE,"E73");var subQ2=makeQuery(id+"F6.imprint","INTERSECT",VERTEX,{"disambiguationData":[OD(0.0)],"derivedFrom":[subQ1,subQ0]});Q5=makeQuery(id+"F6.imprint","IMPRINT",FACE,{"disambiguationData":[TD([[makeQuery(id+"F6.imprint","IMPRINT",EDGE,{"disambiguationData":[TD([[subQ2,-1.0]])],"derivedFrom":subQ1}),-1.0]])]});}
            extrude(context, id + "F7", {"entities" : qUnion([Q0, Q1, Q2, Q3, Q4, Q5]), "operationType" : NewBodyOperationType.ADD, "depth" : 1975 * mm, "offsetDistance" : 25 * mm});
        }
        {
            var Q0;
            {var subQ2=sQuery(id+"F0.wireOp",EDGE,"E3.top");var subQ4=sQuery(id+"F0.wireOp",EDGE,"E2.right");Q0=makeQuery(id+"F3.boolean.opBoolean","SPLIT",FACE,{"disambiguationData":[TD([makeQuery(id+"F1.opExtrude","SWEPT_FACE",FACE,{"disambiguationData":[OSD([subQ4])]})])],"derivedFrom":makeQuery(id+"F1.opExtrude","SWEPT_FACE",FACE,{"disambiguationData":[OSD([subQ2])]})});}
            var sketch = newSketch(context, id + "F8", { "sketchPlane" : qUnion([Q0])});
            skLineSegment(sketch, "E81", {"start": v(12.5, 25) * mm, "end": v(475, 25) * mm});
            skLineSegment(sketch, "E82", {"start": v(475, 25) * mm, "end": v(243.75, 25) * mm});
            skLineSegment(sketch, "E83", {"start": v(243.75, 25) * mm, "end": v(243.75, 0) * mm});
            skLineSegment(sketch, "E84", {"start": v(243.75, 0) * mm, "end": v(12.5, 0) * mm});
            skLineSegment(sketch, "E85", {"start": v(12.5, 0) * mm, "end": v(243.75, 0) * mm});
            skLineSegment(sketch, "E86", {"start": v(475, 0) * mm, "end": v(243.75, 0) * mm});
            skCircle(sketch, "E87", {"center": v(243.75, 12.5) * mm, "radius": 10 * mm});
            skLineSegment(sketch, "E88", {"start": v(128.12, 0) * mm, "end": v(128.12, 25) * mm});
            skLineSegment(sketch, "E89", {"start": v(359.38, 0) * mm, "end": v(359.38, 25) * mm});
            skCircle(sketch, "E90", {"center": v(128.12, 12.5) * mm, "radius": 10 * mm});
            skCircle(sketch, "E91", {"center": v(359.38, 12.5) * mm, "radius": 10 * mm});
            skSolve(sketch);
        }
        {
            var Q0;
            {var subQ0=sQuery(id+"F8.wireOp",EDGE,"E90");var subQ1=sQuery(id+"F8.wireOp",EDGE,"E88");var subQ2=makeQuery(id+"F8.imprint","INTERSECT",VERTEX,{"disambiguationData":[OD(0.0)],"derivedFrom":[subQ1,subQ0]});Q0=makeQuery(id+"F8.imprint","IMPRINT",FACE,{"disambiguationData":[TD([[makeQuery(id+"F8.imprint","IMPRINT",EDGE,{"disambiguationData":[TD([[subQ2,-1.0]])],"derivedFrom":subQ1}),1.0]])]});}
            var Q1;
            {var subQ0=sQuery(id+"F8.wireOp",EDGE,"E90");var subQ1=sQuery(id+"F8.wireOp",EDGE,"E88");var subQ2=makeQuery(id+"F8.imprint","INTERSECT",VERTEX,{"disambiguationData":[OD(0.0)],"derivedFrom":[subQ1,subQ0]});Q1=makeQuery(id+"F8.imprint","IMPRINT",FACE,{"disambiguationData":[TD([[makeQuery(id+"F8.imprint","IMPRINT",EDGE,{"disambiguationData":[TD([[subQ2,-1.0]])],"derivedFrom":subQ1}),-1.0]])]});}
            var Q2;
            {var subQ0=sQuery(id+"F8.wireOp",EDGE,"E91");var subQ1=sQuery(id+"F8.wireOp",EDGE,"E89");var subQ2=makeQuery(id+"F8.imprint","INTERSECT",VERTEX,{"disambiguationData":[OD(0.0)],"derivedFrom":[subQ1,subQ0]});Q2=makeQuery(id+"F8.imprint","IMPRINT",FACE,{"disambiguationData":[TD([[makeQuery(id+"F8.imprint","IMPRINT",EDGE,{"disambiguationData":[TD([[subQ2,-1.0]])],"derivedFrom":subQ1}),1.0]])]});}
            var Q3;
            {var subQ0=sQuery(id+"F8.wireOp",EDGE,"E91");var subQ1=sQuery(id+"F8.wireOp",EDGE,"E89");var subQ2=makeQuery(id+"F8.imprint","INTERSECT",VERTEX,{"disambiguationData":[OD(0.0)],"derivedFrom":[subQ1,subQ0]});Q3=makeQuery(id+"F8.imprint","IMPRINT",FACE,{"disambiguationData":[TD([[makeQuery(id+"F8.imprint","IMPRINT",EDGE,{"disambiguationData":[TD([[subQ2,-1.0]])],"derivedFrom":subQ1}),-1.0]])]});}
            var Q4;
            {var subQ0=sQuery(id+"F8.wireOp",EDGE,"E87");var subQ1=sQuery(id+"F8.wireOp",EDGE,"E83");var subQ2=makeQuery(id+"F8.imprint","INTERSECT",VERTEX,{"disambiguationData":[OD(0.0)],"derivedFrom":[subQ1,subQ0]});Q4=makeQuery(id+"F8.imprint","IMPRINT",FACE,{"disambiguationData":[TD([[makeQuery(id+"F8.imprint","IMPRINT",EDGE,{"disambiguationData":[TD([[subQ2,-1.0]])],"derivedFrom":subQ1}),-1.0]])]});}
            var Q5;
            {var subQ0=sQuery(id+"F8.wireOp",EDGE,"E87");var subQ1=sQuery(id+"F8.wireOp",EDGE,"E83");var subQ2=makeQuery(id+"F8.imprint","INTERSECT",VERTEX,{"disambiguationData":[OD(0.0)],"derivedFrom":[subQ1,subQ0]});Q5=makeQuery(id+"F8.imprint","IMPRINT",FACE,{"disambiguationData":[TD([[makeQuery(id+"F8.imprint","IMPRINT",EDGE,{"disambiguationData":[TD([[subQ2,-1.0]])],"derivedFrom":subQ1}),1.0]])]});}
            extrude(context, id + "F9", {"entities" : qUnion([Q0, Q1, Q2, Q3, Q4, Q5]), "operationType" : NewBodyOperationType.ADD, "depth" : 1975 * mm, "offsetDistance" : 25 * mm});
        }
        {
            var Q0;
            Q0=makeQuery(id+"F5.opExtrude","CAP_FACE",FACE,{"disambiguationData":[OSD([sQuery(id+"F0.wireOp",EDGE,"E2.left"),sQuery(id+"F0.wireOp",EDGE,"E3.left"),sQuery(id+"F4.wireOp",EDGE,"E13"),sQuery(id+"F4.wireOp",EDGE,"E16"),sQuery(id+"F4.wireOp",EDGE,"E38"),sQuery(id+"F4.wireOp",EDGE,"E39"),sQuery(id+"F4.wireOp",EDGE,"E45"),sQuery(id+"F4.wireOp",EDGE,"E46"),sQuery(id+"F4.wireOp",EDGE,"E54"),sQuery(id+"F4.wireOp",EDGE,"E56"),sQuery(id+"F4.wireOp",EDGE,"E58"),sQuery(id+"F4.wireOp",EDGE,"E69"),sQuery(id+"F4.wireOp",EDGE,"E70")])],"isStart":false});
            var sketch = newSketch(context, id + "F10", { "sketchPlane" : qUnion([Q0])});
            skLineSegment(sketch, "E92", {"start": v(175, 987.5) * mm, "end": v(500, 1312.5) * mm});
            skLineSegment(sketch, "E93", {"start": v(500, 1312.5) * mm, "end": v(175, 987.5) * mm});
            skLineSegment(sketch, "E94", {"start": v(175, 987.5) * mm, "end": v(500, 662.5) * mm});
            skPoint(sketch, "E95.oppositeSnap0", {"position": v(337.5, 1150) * mm});
            skLineSegment(sketch, "E95.bottom", {"start": v(337.5, 825) * mm, "end": v(500, 825) * mm});
            skLineSegment(sketch, "E95.top", {"start": v(337.5, 1150) * mm, "end": v(500, 1150) * mm});
            skLineSegment(sketch, "E95.left", {"start": v(337.5, 825) * mm, "end": v(337.5, 1150) * mm});
            skLineSegment(sketch, "E95.right", {"start": v(500, 825) * mm, "end": v(500, 1150) * mm});
            skSolve(sketch);
        }
        {
            var Q0;
            Q0=makeQuery(id+"F10.imprint","IMPRINT",FACE,{"disambiguationData":[TD([[makeQuery(id+"F10.imprint","IMPRINT",EDGE,{"derivedFrom":sQuery(id+"F10.wireOp",EDGE,"E95.bottom")}),1.0]])]});
            extrude(context, id + "F11", {"entities" : qUnion([Q0]), "operationType" : NewBodyOperationType.ADD, "depth" : 5 * mm, "offsetDistance" : 25 * mm});
        }
        {
            var Q0;
            Q0=makeQuery(id+"F11.opExtrude","CAP_FACE",FACE,{"disambiguationData":[OSD([sQuery(id+"F10.wireOp",EDGE,"E95.bottom"),sQuery(id+"F10.wireOp",EDGE,"E95.top"),sQuery(id+"F10.wireOp",EDGE,"E95.left"),sQuery(id+"F10.wireOp",EDGE,"E95.right")])],"isStart":false});
            var sketch = newSketch(context, id + "F12", { "sketchPlane" : qUnion([Q0])});
            skLineSegment(sketch, "E96", {"start": v(337.5, 1150) * mm, "end": v(500, 825) * mm, "construction": true});
            skLineSegment(sketch, "E97", {"start": v(500, 825) * mm, "end": v(337.5, 825) * mm, "construction": true});
            skLineSegment(sketch, "E98", {"start": v(337.5, 825) * mm, "end": v(500, 1150) * mm, "construction": true});
            skLineSegment(sketch, "E99.bottom", {"start": v(431.25, 1012.5) * mm, "end": v(406.25, 1012.5) * mm, "construction": true});
            skLineSegment(sketch, "E99.top", {"start": v(431.25, 962.5) * mm, "end": v(406.25, 962.5) * mm});
            skLineSegment(sketch, "E99.left", {"start": v(431.25, 1012.5) * mm, "end": v(431.25, 962.5) * mm});
            skLineSegment(sketch, "E99.right", {"start": v(406.25, 1012.5) * mm, "end": v(406.25, 962.5) * mm});
            skPoint(sketch, "E99.middle", {"position": v(418.75, 987.5) * mm});
            skCircle(sketch, "E100", {"center": v(418.75, 1012.5) * mm, "radius": 18.75 * mm});
            skSolve(sketch);
        }
        {
            var Q0;
            Q0 = qSketchRegion(id + "F12", true);
            extrude(context, id + "F13", {"entities" : qUnion([Q0]), "operationType" : NewBodyOperationType.REMOVE, "oppositeDirection" : true, "depth" : 86.3 * mm, "offsetDistance" : 25 * mm});
        }
    });
